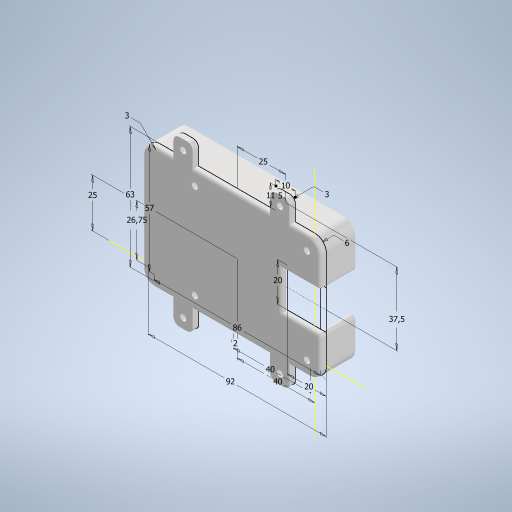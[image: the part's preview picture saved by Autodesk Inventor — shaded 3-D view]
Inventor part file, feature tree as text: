
AUTODESK INVENTOR PART (.ipt)
format: ipt  version: 2024.3 (Build 283343000, 343)  size: 474,624 bytes
history: native  units: in
note: dims shown in document units (in); Inventor stores cm internally (conversion verified against a paired STEP export)
features: extrude x4, sketch x2, fillet x1, hole x1
ambient origin geometry x8: Origin, YZ Plane, XZ Plane, XY Plane, X Axis, Y Axis, Z Axis, Center Point
bodies: Solid1 (feature_tree)
feature tree (8):
  sketch  "Sketch1"  dims[d0=3.622in d1=2.4803in]
  extrude  "Extrusion1"  Depth=2.4803in
  sketch  "Sketch2"  dims[d2=0.9843in d3=1.5748in d5=0.1181in d6=0.0in d7=0.126in d8=1.9488in d9=0.126in d10=0.0197in d11=0.126in d12=2.2835in d13=0.126in d14=0.0394in d15=3.3858in d16=2.2441in d17=0.1181in d18=0.2362in d19=1.0531in d20=0.7874in d21=0.7874in d22=1.5748in d23=0.0787in d24=0.5906in d25=0.0in d26=0.0591in d27=0.2362in d28=0.2362in d29=0.2362in d30=0.2362in d31=0.1181in d32=0.0in d33=0.0in d34=0.0in d37=0.3937in d38=0.4331in d39=0.9843in d40=1.4764in d41=0.1969in d42=0.1181in d43=0.126in d44=0.2362in d45=0.1575in d46=0.0787in d47=90.0deg d48=0.315in d49=0.8108in]
  extrude  "Extrusion2"  Depth=0.2362in
  fillet  "Fillet1"  Radius=0.1181in
  extrude  "Extrusion3"  Depth=0.2362in
  extrude  "Extrusion4"  Depth=0.2362in
  hole  "Hole1"  [1 undecoded]
note: 1 required parameter value undecoded (feature->parameter linkage not recoverable at this tier; creation-order binding heuristic only, values carry confidence <= 0.55)
